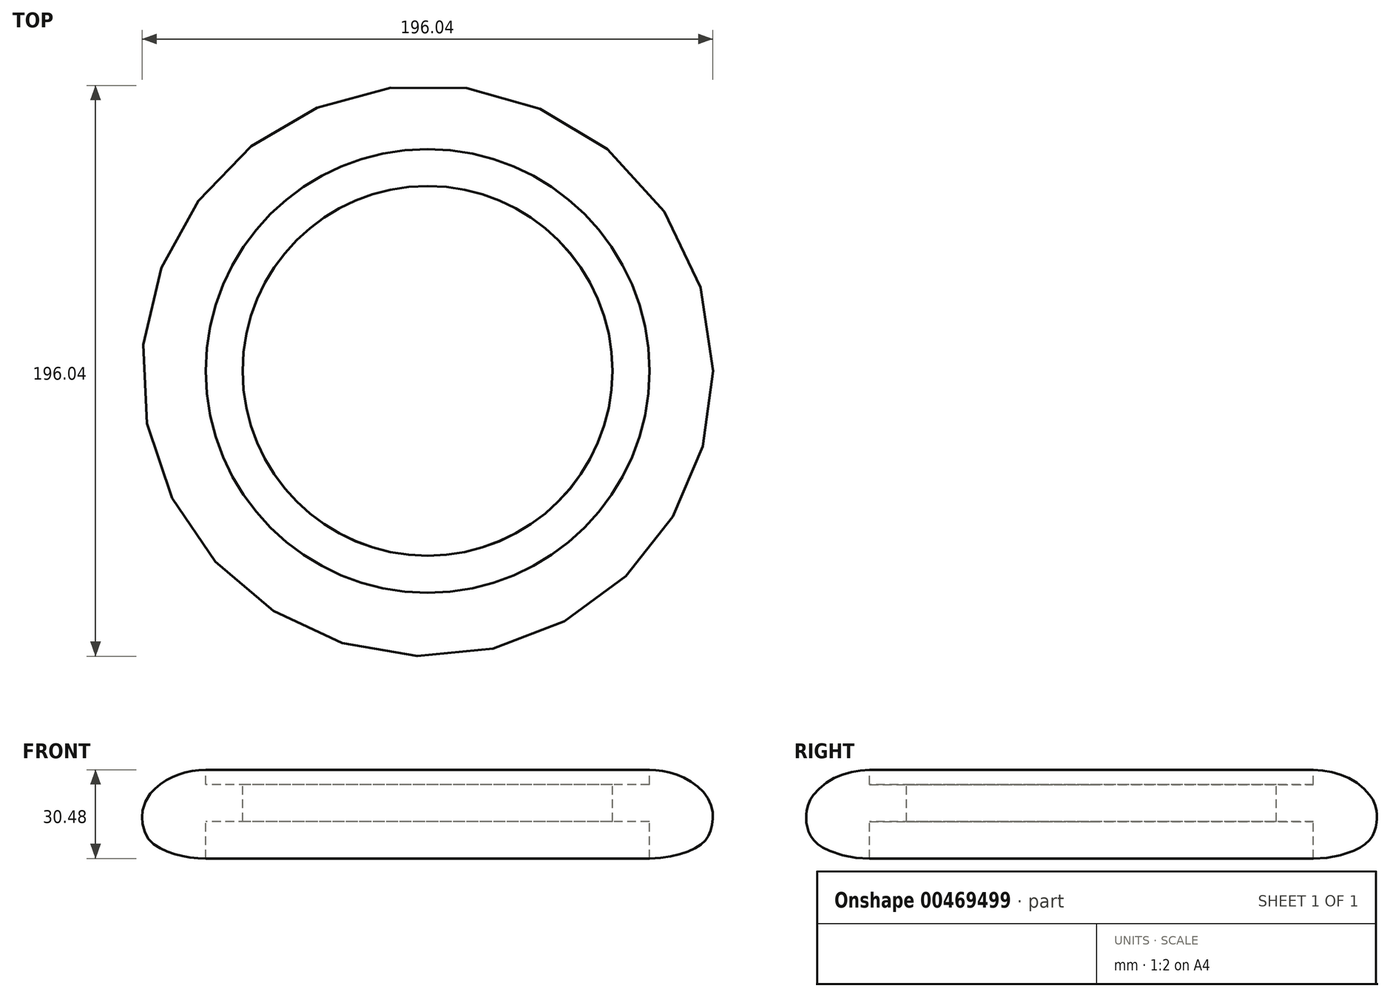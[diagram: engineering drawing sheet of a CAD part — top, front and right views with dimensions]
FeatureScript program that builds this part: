
annotation { "Feature Type Name" : "Feature", "Feature Type Description" : "" }
export const myFeature = defineFeature(function(context is Context, id is Id, definition is map)
    precondition{}
    {
        {
            var Q0;
            Q0=qCreatedBy(makeId("Front.planeOp"),FACE);
            var sketch = newSketch(context, id + "F0", { "sketchPlane" : qUnion([Q0])});
            skLineSegment(sketch, "E0", {"start": v(0, 0) * mm, "end": v(-63.5, 0) * mm, "construction": true});
            skLineSegment(sketch, "E1", {"start": v(-63.5, 0) * mm, "end": v(-63.5, 31.75) * mm, "construction": true});
            skSolve(sketch);
        }
        {
            var Q0;
            Q0=qCreatedBy(makeId("Front.planeOp"),FACE);
            var sketch = newSketch(context, id + "F1", { "sketchPlane" : qUnion([Q0])});
            skLineSegment(sketch, "E2", {"start": v(-63.5, 12.7) * mm, "end": v(-76.2, 12.7) * mm});
            skLineSegment(sketch, "E3", {"start": v(-76.2, 12.7) * mm, "end": v(-76.2, 0) * mm});
            skLineSegment(sketch, "E4", {"start": v(-63.52, 25.4) * mm, "end": v(-76.22, 25.4) * mm});
            skLineSegment(sketch, "E5", {"start": v(-76.22, 25.4) * mm, "end": v(-76.22, 30.48) * mm});
            skFitSpline(sketch, "E6", {"points": [v(-76.22, 30.48) * mm, v(-86.76, 28.35) * mm, v(-96.84, 19.64) * mm, v(-97.44, 10.07) * mm, v(-93.41, 4.47) * mm, v(-76.2, 0) * mm], "startDerivative": vector(-46.8, -2.55) * mm, "endDerivative": vector(90, 0) * mm});
            skLineSegment(sketch, "E7", {"start": v(-63.52, 25.4) * mm, "end": v(-63.5, 12.7) * mm});
            skLineSegment(sketch, "E8", {"start": v(0, 38.42) * mm, "end": v(0, 0) * mm, "construction": true});
            skSolve(sketch);
        }
        {
            var Q0;
            Q0=makeQuery(id+"F1.imprint","IMPRINT",FACE,{"disambiguationData":[TD([[makeQuery(id+"F1.imprint","IMPRINT",EDGE,{"derivedFrom":sQuery(id+"F1.wireOp",EDGE,"E2")}),-1.0]])]});
            var Q1;
            Q1=sQuery(id+"F1.wireOp",EDGE,"E8");
            revolve(context, id + "F2", {"entities" : qUnion([Q0]), "axis" : qUnion([Q1]), "revolveType" : RevolveType.FULL});
        }
    });
